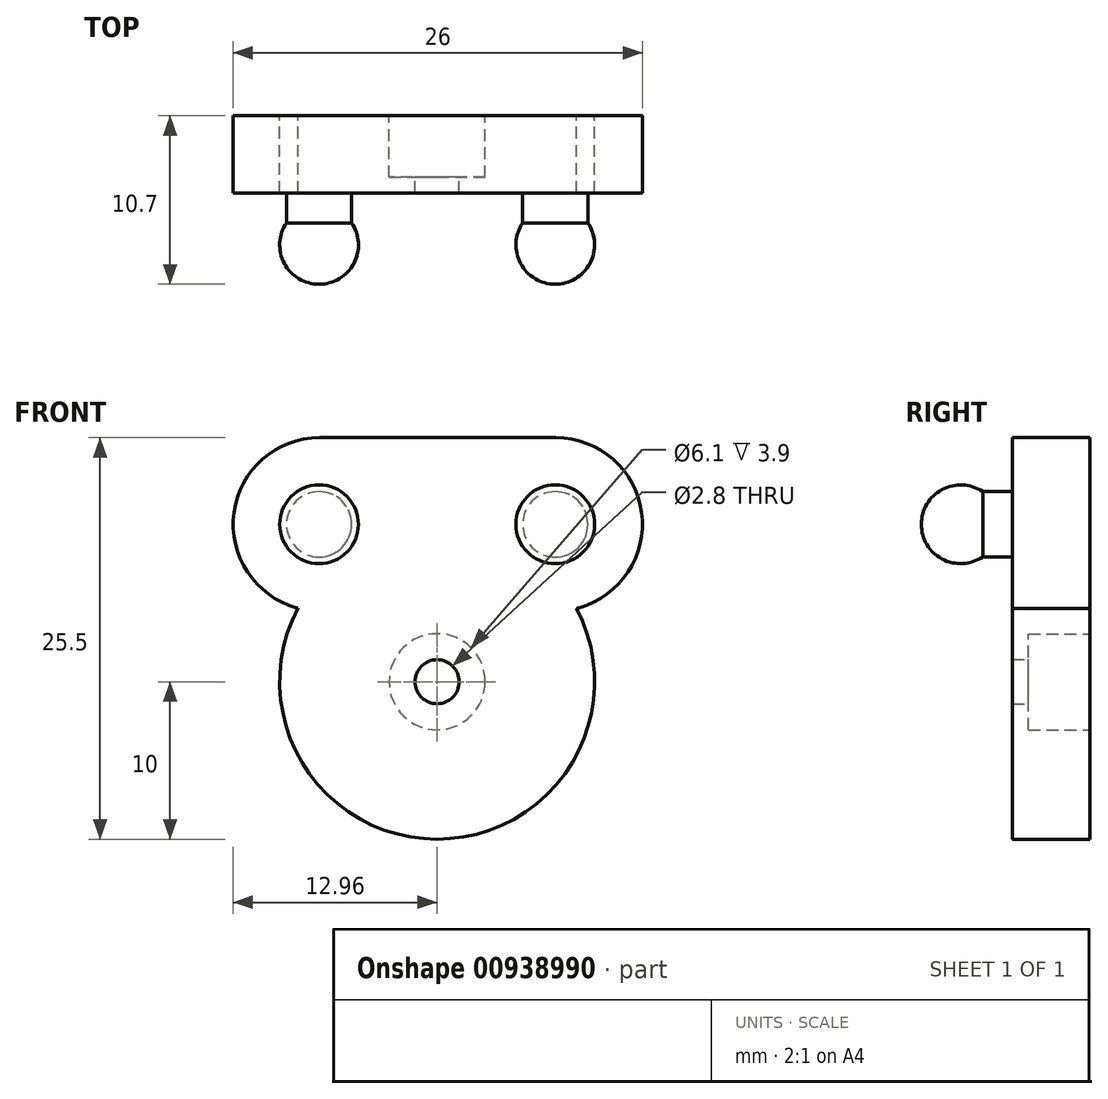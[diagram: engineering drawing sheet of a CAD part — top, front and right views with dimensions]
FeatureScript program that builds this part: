
annotation { "Feature Type Name" : "Feature", "Feature Type Description" : "" }
export const myFeature = defineFeature(function(context is Context, id is Id, definition is map)
    precondition{}
    {
        {
            var Q0;
            Q0=qCreatedBy(makeId("Front.planeOp"),FACE);
            var sketch = newSketch(context, id + "F0", { "sketchPlane" : qUnion([Q0])});
            skCircle(sketch, "E0", {"center": v(0, 0) * mm, "radius": 3.05 * mm});
            skCircle(sketch, "E1", {"center": v(0, 0) * mm, "radius": 10 * mm});
            skLineSegment(sketch, "E2", {"start": v(0, 0) * mm, "end": v(0, 10) * mm, "construction": true});
            skLineSegment(sketch, "E3", {"start": v(-7.46, 10) * mm, "end": v(7.54, 10) * mm});
            skCircle(sketch, "E4", {"center": v(-7.46, 10) * mm, "radius": 5.5 * mm, "construction": true});
            skCircle(sketch, "E5", {"center": v(7.54, 10) * mm, "radius": 5.5 * mm, "construction": true});
            skLineSegment(sketch, "E6", {"start": v(0, 10) * mm, "end": v(0, 15.5) * mm, "construction": true});
            skLineSegment(sketch, "E7", {"start": v(-7.46, 15.5) * mm, "end": v(7.54, 15.5) * mm});
            skArc(sketch, "E8", {"start": v(-7.46, 15.5) * mm, "mid": v(-12.91, 10.74) * mm, "end": v(-8.93, 4.7) * mm});
            skArc(sketch, "E9", {"start": v(9, 4.7) * mm, "mid": v(12.99, 10.74) * mm, "end": v(7.54, 15.5) * mm});
            skLineSegment(sketch, "E10", {"start": v(-7.46, 6.66) * mm, "end": v(-7.46, 2.77) * mm});
            skLineSegment(sketch, "E11", {"start": v(7.54, 6.57) * mm, "end": v(7.54, 2.77) * mm});
            skPoint(sketch, "E12.visualSharp", {"position": v(-7.46, 4.5) * mm});
            skArc(sketch, "E12.filletArc", {"start": v(-7.46, 2.77) * mm, "mid": v(-7.87, 3.98) * mm, "end": v(-8.93, 4.7) * mm});
            skPoint(sketch, "E13.visualSharp", {"position": v(7.54, 4.5) * mm});
            skArc(sketch, "E13.filletArc", {"start": v(9, 4.7) * mm, "mid": v(7.95, 3.98) * mm, "end": v(7.54, 2.77) * mm});
            skSolve(sketch);
        }
        {
            var Q0;
            Q0=makeQuery(id+"F0.imprint","IMPRINT",FACE,{"disambiguationData":[TD([[makeQuery(id+"F0.imprint","IMPRINT",EDGE,{"derivedFrom":sQuery(id+"F0.wireOp",EDGE,"E7")}),-1.0]])]});
            var Q1;
            {var subQ0=sQuery(id+"F0.wireOp",EDGE,"E10");Q1=makeQuery(id+"F0.imprint","IMPRINT",FACE,{"disambiguationData":[TD([[makeQuery(id+"F0.imprint","IMPRINT",EDGE,{"derivedFrom":subQ0}),-1.0]])]});}
            var Q2;
            Q2=makeQuery(id+"F0.imprint","IMPRINT",FACE,{"disambiguationData":[TD([[makeQuery(id+"F0.imprint","IMPRINT",EDGE,{"derivedFrom":sQuery(id+"F0.wireOp",EDGE,"E0")}),-1.0]])]});
            var Q3;
            {var subQ0=sQuery(id+"F0.wireOp",EDGE,"E11");Q3=makeQuery(id+"F0.imprint","IMPRINT",FACE,{"disambiguationData":[TD([[makeQuery(id+"F0.imprint","IMPRINT",EDGE,{"derivedFrom":subQ0}),1.0]])]});}
            extrude(context, id + "F1", {"entities" : qUnion([Q0, Q1, Q2, Q3]), "depth" : 3.9 * mm, "offsetDistance" : 25 * mm});
        }
        {
            var Q0;
            Q0=makeQuery(id+"F1.opExtrude","CAP_FACE",FACE,{"disambiguationData":[OSD([sQuery(id+"F0.wireOp",EDGE,"E0"),sQuery(id+"F0.wireOp",EDGE,"E1"),sQuery(id+"F0.wireOp",EDGE,"Ro747M3z-J5t0-M7PT-VmPf-xVWHkuJRowBz"),sQuery(id+"F0.wireOp",EDGE,"dBziJt0X-J2fB-U4kL-1lBP-q9dJNjyh9b4h"),sQuery(id+"F0.wireOp",EDGE,"E7"),sQuery(id+"F0.wireOp",EDGE,"E8"),sQuery(id+"F0.wireOp",EDGE,"E9"),sQuery(id+"F0.wireOp",EDGE,"E10"),sQuery(id+"F0.wireOp",EDGE,"E11"),sQuery(id+"F0.wireOp",EDGE,"E12.filletArc"),sQuery(id+"F0.wireOp",EDGE,"E13.filletArc")])],"isStart":false});
            var sketch = newSketch(context, id + "F2", { "sketchPlane" : qUnion([Q0])});
            skCircle(sketch, "E14", {"center": v(0, 0) * mm, "radius": 1.4 * mm});
            skSolve(sketch);
        }
        {
            var Q0;
            Q0=makeQuery(id+"F2.imprint","IMPRINT",FACE,{"disambiguationData":[TD([[makeQuery(id+"F2.imprint","IMPRINT",EDGE,{"derivedFrom":makeQuery(id+"F1.opExtrude","CAP_EDGE",EDGE,{"disambiguationData":[OSD([sQuery(id+"F0.wireOp",EDGE,"E0")])],"isStart":false})}),-1.0]])]});
            var Q1;
            Q1=makeQuery(id+"F2.imprint","IMPRINT",FACE,{"disambiguationData":[TD([[makeQuery(id+"F2.imprint","IMPRINT",EDGE,{"derivedFrom":sQuery(id+"F2.wireOp",EDGE,"E14")}),-1.0]])]});
            extrude(context, id + "F3", {"entities" : qUnion([Q0, Q1]), "operationType" : NewBodyOperationType.ADD, "depth" : 1 * mm, "offsetDistance" : 25 * mm});
        }
        {
            var Q0;
            Q0=qCreatedBy(makeId("Top.planeOp"),FACE);
            cPlane(context, id + "F4", {"entities" : qUnion([Q0]), "cplaneType" : CPlaneType.OFFSET, "offset" : 10 * mm, "width" : 150 * mm, "height" : 150 * mm});
        }
        {
            var Q0;
            Q0=qCreatedBy(id+"F4.planeOp",FACE);
            var sketch = newSketch(context, id + "F5", { "sketchPlane" : qUnion([Q0])});
            skArc(sketch, "E15", {"start": v(-7.5, -10.7) * mm, "mid": v(-5, -8.2) * mm, "end": v(-7.5, -5.7) * mm});
            skPoint(sketch, "E16.end.orphan", {"position": v(0, 0.2) * mm});
            skLineSegment(sketch, "E17", {"start": v(-7.5, 0.2) * mm, "end": v(-7.5, -10) * mm, "construction": true});
            skArc(sketch, "E18", {"start": v(7.5, -10.7) * mm, "mid": v(10, -8.2) * mm, "end": v(7.5, -5.7) * mm});
            skLineSegment(sketch, "E19", {"start": v(7.5, 0.37) * mm, "end": v(7.5, -9.83) * mm, "construction": true});
            skLineSegment(sketch, "E20", {"start": v(-7.5, -8.2) * mm, "end": v(10.97, -8.2) * mm, "construction": true});
            skLineSegment(sketch, "E21", {"start": v(-9.57, -6.8) * mm, "end": v(9.57, -6.8) * mm, "construction": true});
            skLineSegment(sketch, "E22", {"start": v(-5.43, -6.8) * mm, "end": v(-5.43, -4.8) * mm});
            skLineSegment(sketch, "E23", {"start": v(9.57, -6.8) * mm, "end": v(9.57, -4.78) * mm});
            skLineSegment(sketch, "E24", {"start": v(-7.5, -4.8) * mm, "end": v(-5.43, -4.8) * mm});
            skLineSegment(sketch, "E25", {"start": v(9.57, -4.78) * mm, "end": v(7.5, -4.78) * mm});
            skLineSegment(sketch, "E26", {"start": v(-7.5, -10.7) * mm, "end": v(-7.5, -4.9) * mm});
            skLineSegment(sketch, "E27", {"start": v(7.5, -10.7) * mm, "end": v(7.5, -4.73) * mm});
            skLineSegment(sketch, "E28", {"start": v(-7.5, -4.8) * mm, "end": v(-7.5, -4.9) * mm});
            skSolve(sketch);
        }
        {
            var Q0;
            {var subQ0=sQuery(id+"F5.wireOp",EDGE,"E26");var subQ1=sQuery(id+"F5.wireOp",EDGE,"E15");var subQ2=makeQuery(id+"F5.imprint","INTERSECT",VERTEX,{"disambiguationData":[OD(0.0)],"derivedFrom":[subQ1,subQ0]});Q0=makeQuery(id+"F5.imprint","IMPRINT",FACE,{"disambiguationData":[TD([[makeQuery(id+"F5.imprint","IMPRINT",EDGE,{"disambiguationData":[TD([[subQ2,-1.0]])],"derivedFrom":subQ1}),1.0]])]});}
            var Q1;
            {var subQ4=sQuery(id+"F5.wireOp",EDGE,"E22");Q1=makeQuery(id+"F5.imprint","IMPRINT",FACE,{"disambiguationData":[TD([[makeQuery(id+"F5.imprint","IMPRINT",EDGE,{"derivedFrom":subQ4}),1.0]])]});}
            var Q2;
            Q2=sQuery(id+"F5.wireOp",EDGE,"E17");
            revolve(context, id + "F6", {"operationType" : NewBodyOperationType.ADD, "surfaceOperationType" : NewSurfaceOperationType.NEW, "entities" : qUnion([Q0, Q1]), "axis" : qUnion([Q2]), "revolveType" : RevolveType.FULL});
        }
        {
            var Q0;
            {var subQ3=sQuery(id+"F5.wireOp",EDGE,"E23");Q0=makeQuery(id+"F5.imprint","IMPRINT",FACE,{"disambiguationData":[TD([[makeQuery(id+"F5.imprint","IMPRINT",EDGE,{"derivedFrom":subQ3}),1.0]])]});}
            var Q1;
            {var subQ0=sQuery(id+"F5.wireOp",EDGE,"E27");var subQ1=sQuery(id+"F5.wireOp",EDGE,"E18");var subQ2=makeQuery(id+"F5.imprint","INTERSECT",VERTEX,{"disambiguationData":[OD(0.0)],"derivedFrom":[subQ1,subQ0]});Q1=makeQuery(id+"F5.imprint","IMPRINT",FACE,{"disambiguationData":[TD([[makeQuery(id+"F5.imprint","IMPRINT",EDGE,{"disambiguationData":[TD([[subQ2,-1.0]])],"derivedFrom":subQ1}),1.0]])]});}
            var Q2;
            Q2=sQuery(id+"F5.wireOp",EDGE,"E19");
            revolve(context, id + "F7", {"operationType" : NewBodyOperationType.ADD, "surfaceOperationType" : NewSurfaceOperationType.NEW, "entities" : qUnion([Q0, Q1]), "axis" : qUnion([Q2]), "revolveType" : RevolveType.FULL});
        }
    });
